# Revit family: Haworth_Immerse_SingleTable_Racetrack
name_source: partatom
category: Furniture Systems
revit_build: Autodesk Revit 2018 (Build: 20170223_1515(x64)
units: mm (PartAtom-declared; Revit-internal decimal feet)

## family parameters
Always vertical = Yes
Cut with Voids When Loaded = No
OmniClass Number = 23.40.70.14.64.21
OmniClass Title = Systems Furniture
Part Type = Normal
Room Calculation Point = No
Round Connector Dimension = Use Diameter
Shared = No
Work Plane-Based = No

## types (6) — shared parameters
Actual Depth = 48"
Actual Width = 96"
Assembly Code = E2020200
Lower Top Cutout Depth = 12 1/2"
Lower Top Cutout Width = 54"
Lower Top Thickness = 1/8"
Lower Top Width = 94"
Manufacturer = Haworth
Model = THRT-4896
Revision Number = 1
Size = Verify Final Dim. w/ Haworth
Standard Depths = 48 in.
Standard Heights = 29, 36, 39 in.
Standard Widths = 96 in.
URL = https://www.haworth.com
URL - Product = http://www.haworth.com
Understructure Overall Width = 57"
Understucture Thickness = 3 1/2"
Upper Top Thickness = 1 3/16"
Warranty = http://www.haworth.com

## per-type parameters (varying)
| type | Actual Height | Description | Oblong Planter | Oblong Planter Void Height |
| 48d 96w 39h - Oblong Planter | 39" | Haworth Immerse Single Table Racetrack - 48d 96w 39h - Oblong Planter | Yes | 30" |
| 48d 96w 36h - Oblong Planter | 36" | Haworth Immerse Single Table Racetrack - 48d 96w 36h - Oblong Planter | Yes | 30" |
| 48d 96w 29h - Oblong Planter | 29" | Haworth Immerse Single Table Racetrack - 48d 96w 29h - Oblong Planter | Yes | 30" |
| 48d 96w 29h - No Planter | 29" | Haworth Immerse Single Table Racetrack - 48d 96w 29h - No Planter | No | 1" |
| 48d 96w 36h - No Planter | 36" | Haworth Immerse Single Table Racetrack - 48d 96w 36h - No Planter | No | 1" |
| 48d 96w 39h - No Planter | 39" | Haworth Immerse Single Table Racetrack - 48d 96w 39h - No Planter | No | 1" |

## geometry (parser evidence)
native form markers: Sweep x6
no freeform markers — native parametric forms only
